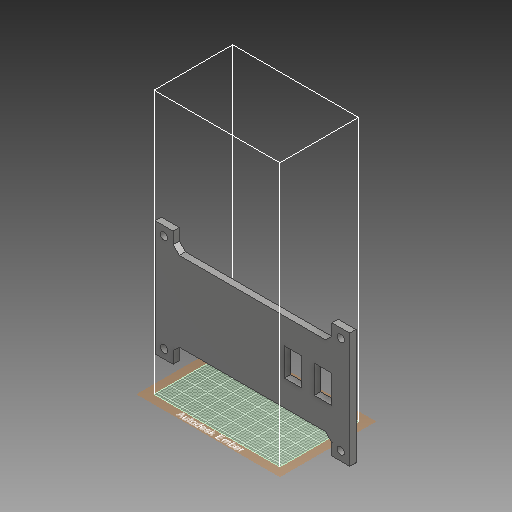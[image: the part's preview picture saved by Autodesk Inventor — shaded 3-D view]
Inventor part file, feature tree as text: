
AUTODESK INVENTOR PART (.ipt)
format: ipt  version: 2018 (Build 220112000, 112)  size: 1,635,840 bytes
history: native  units: in
note: dims shown in document units (in); Inventor stores cm internally (conversion verified against a paired STEP export)
features: sketch x6, extrude x4, move_body x3, emboss x2, direct_edit x2, chamfer x1
ambient origin geometry x8: Origin, YZ Plane, XZ Plane, XY Plane, X Axis, Y Axis, Z Axis, Center Point
bodies: Solid1 (feature_tree)
feature tree (18):
  extrude  "Extrusion1"  Depth=0.36in
  extrude  "Extrusion2"  Depth=0.36in
  extrude  "Extrusion3"  Depth=0.36in
  emboss  "Emboss1"
  emboss  "Emboss2"
  extrude  "Extrusion4"  Depth=0.125in TaperAngle=0.0deg
  chamfer  "Chamfer1"  Distance=0.146in
  direct_edit  "Direct Edit1"
  direct_edit  "Direct Edit2"
  sketch  "Sketch1"  dims[d0=2.311in d1=0.36in]
  sketch  "Sketch2"  dims[d2=0.36in d3=0.36in]
  sketch  "Sketch3"  dims[d4=0.36in d5=0.36in]
  sketch  "Sketch5"  dims[d7=0.36in d8=0.125in d9=0.0in]
  sketch  "Sketch6"  dims[d10=0.146in]
  sketch  "Sketch7"  dims[d11=0.146in d12=0.146in d13=0.146in d14=1.0in d15=0.0in d16=3.9in d17=0.18in d18=0.181in d19=0.18in d20=0.18in d21=0.181in d22=0.18in d23=0.18in d24=0.18in d25=0.56in d26=0.35in d27=0.35in d28=0.25in d30=1.0in d31=0.0in d32=0.36in d34=270.0deg d35=270.0deg d37=0.02in d38=0.0in d39=0.033in d40=0.025in d41=0.1in d42=1.2in d43=0.025in d44=0.0325in d45=45.0deg d46=0.4in d47=0.2in d48=0.175in d49=0.175in d50=1.0625in d51=0.045in d52=0.0329in d53=0.045in d54=0.0325in d55=0.045in d56=0.0in d59=270.0deg d60=0.03in d61=0.0in d62=1.0in d63=0.0in d64=0.125in d65=0.125in d66=45.0deg d67=0.0in d68=0.0in d69=0.105in d70=0.0in d71=0.0in d72=0.105in d73=-0.1in d74=0.0in d75=0.0in]
  move_body  "Move1"
  move_body  "Move2"
  move_body  "Move3"
